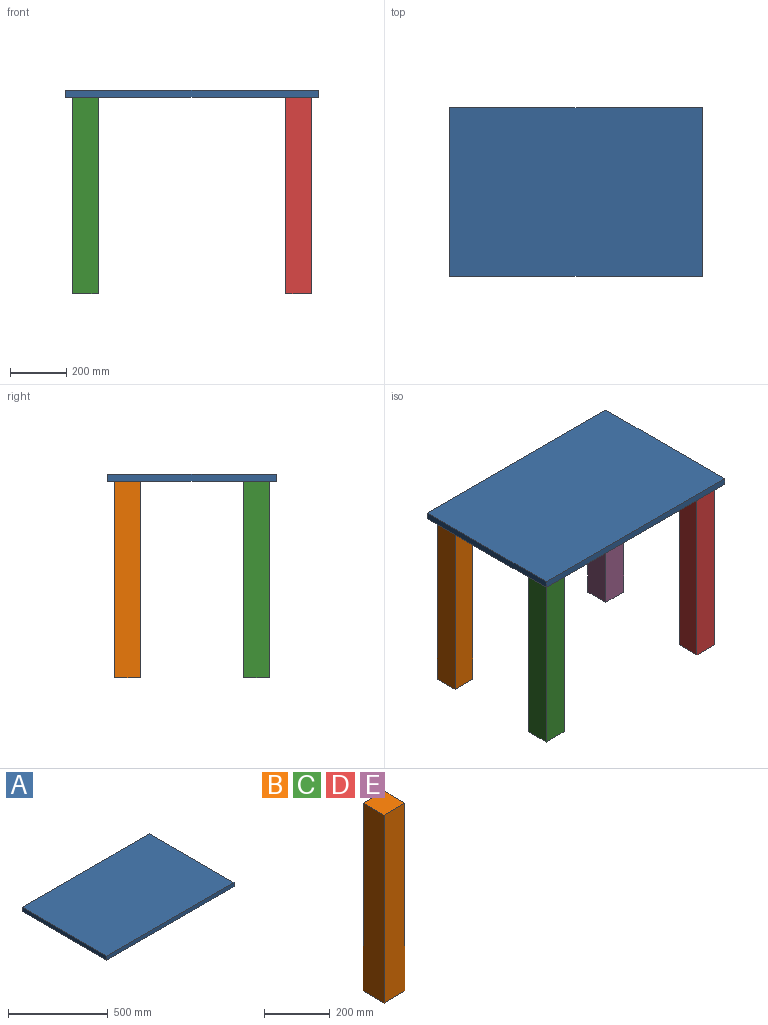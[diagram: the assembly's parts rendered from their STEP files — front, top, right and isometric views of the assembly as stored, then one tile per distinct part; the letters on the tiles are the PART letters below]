
ASSEMBLY  parts=5 mates=4
PART A: 6 faces, bbox 900x600x25 mm
  f0: plane 900x25mm, normal (0,-1,0), area 22500mm2, adj f1,f3,f4,f5
  f1: plane 600x25mm, normal (1,0,0), area 15000mm2, adj f0,f2,f4,f5
  f2: plane 900x25mm, normal (0,1,0), area 22500mm2, adj f1,f3,f4,f5
  f3: plane 600x25mm, normal (-1,0,0), area 15000mm2, adj f0,f2,f4,f5
  f4: plane 900x600mm, normal (0,0,1), area 540000mm2, adj f0,f1,f2,f3
  f5: plane 900x600mm, normal (0,0,-1), area 540000mm2, adj f0,f1,f2,f3
PART B: 6 faces, bbox 90x90x700 mm
  f0: plane 700x90mm, normal (-1,0,0), area 63000mm2, adj f1,f3,f4,f5
  f1: plane 700x90mm, normal (0,-1,0), area 63000mm2, adj f0,f2,f4,f5
  f2: plane 700x90mm, normal (1,0,0), area 63000mm2, adj f1,f3,f4,f5
  f3: plane 700x90mm, normal (0,1,0), area 63000mm2, adj f0,f2,f4,f5
  f4: plane 90x90mm, normal (0,0,1), area 8100mm2, adj f0,f1,f2,f3
  f5: plane 90x90mm, normal (0,0,-1), area 8100mm2, adj f0,f1,f2,f3
PART C: same geometry as B
PART D: same geometry as B
PART E: same geometry as B
PLACE A t=(1.76,1.74,-11.42)mm fixed
PLACE B t=(-423.24,276.74,-711.42)mm
PLACE C t=(-423.24,-183.26,-711.42)mm
PLACE D t=(336.76,-183.26,-711.42)mm
PLACE E t=(336.76,276.74,-711.42)mm
MATE fastened E.f4 <-> A.f5  axis (0,0,1) through (426.76,186.74,-11.42)mm
MATE fastened A.f5 <-> C.f4  axis (0,0,1) through (-448.24,-298.26,-11.42)mm
MATE fastened B.f4 <-> A.f5  axis (0,0,1) through (-423.24,186.74,-11.42)mm
MATE fastened D.f4 <-> A.f5  axis (0,0,1) through (336.76,-273.26,-11.42)mm
